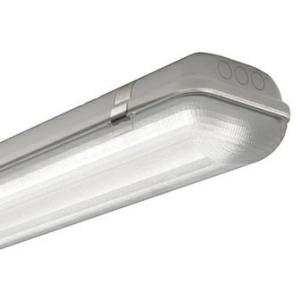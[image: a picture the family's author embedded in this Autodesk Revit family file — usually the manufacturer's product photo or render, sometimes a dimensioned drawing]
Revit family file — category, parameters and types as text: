
# Revit family: 3f_filippi_-_3f_linda_3f_filippi_-_58600_-_3f_linda_led_2x24w_ep_l1270
name_source: partatom
category: Lighting Fixtures
units: mm (PartAtom-declared; Revit-internal decimal feet)

## family parameters
Cut with Voids When Loaded = No
Host = Face
Light Source = No
Part Type = Normal
Room Calculation Point = No
Round Connector Dimension = Use Diameter
Shared = No

## types (1)
- 3F Filippi - 3F Linda (1 x LED, 7911 lm, 55.5 W, 4000 K)
    Apparent Load = 56 VA
    Approval mark = ENEC
    CIE Flux Codes = 46 76 93 97 100
    Color Rendering = 80
    Color Temperature = 4000 K
    Control Gear = Electronic ballast
    Default Elevation = 1800 mm
    Description = ILLUMINOTECHNICAL
Luminous efficiency 100% (DLOR 97%, ULOR 3%).
Initial luminous flux of the luminaire 7911 lm.
Emergency luminaire luminous flux BLF 7.1%.
Controlled symmetric distribution.
Installation Interdistance Transv.D = 1.52 x hu - Long.D = 1.17 x hu.
Tabular UGR (CIE 117 - 4H-8H; S=0.25H; 70/50/20): RUG 24.4 - 23.5.
Beam angle: 94° - 78°.
Luminous efficacy 143 lm/W.
Lifetime (L93/B10): 30000 h. (tq+25°C)
Lifetime (L90/B10): 50000 h. (tq+25°C)
Lifetime (L85/B10): 80000 h. (tq+25°C)
Lifetime (L80/B10): 100000 h. (tq+25°C)
Sudden decreased luminous flux after 50000 hours: 0% (C0).
Photobiological safety in compliance with IEC/TR 62778: RG0 risk exempt, (IEC 62471).
In compliance with IEC/EN 62722-2-1 - IEC/EN 62717 standards.

SOURCE
2 linear LED modules 24W/840.
Energy efficiency class (UE 2019/2020 - UE 2019/2015): D.
CIE 13.3 Colour rendering index: CRI >80 (R9 <50%).
IES TM-30 Fidelity Index: Rf = 84 Rg = 95.
CCT nominal colour temperature 4000 K.
Colour initial tolerance (MacAdam): SDCM 3.

MECHANICAL
Self-extinguishing V2 polycarbonate housing, injection moulded, RAL 7035 grey.
Ecologic anti-aging injected sealing gasket.
Diffuser in self-extinguishing V2 polycarbonate, photo-engraved interior, UV stabilised, injection moulded with smooth outer surface, tamper-proof opening.
Gear-holder reflector in hot-dip galvanised steel, painted with white polyester base.
Snug fit safety snap-lock clips for diffuser mounting in stainless steel, screwdriver opening.
Fixing brackets in stainless steel.
Possibility for technicians to access the interior of the luminaire.
Luminaire with limited surface temperature. - D - (EN 60598-2-24)
Dimensions: 1270x160 mm, height 100 mm. Weight 3.294 kg.
IP66 protection degree.
Mechanical strength to impacts IK10 (20 joule).
Glow-wire test resistance 850°C.

ELECTRICAL
Halogen Free electronic wiring 230V-50/60Hz, power factor 0.90, THD <25%, constant output current, SELV, class I, 1 driver.
Power of the luminaire 55.5 W.
CE - IEC 60598-1 - EN 60598-1.
EP maintained emergency wiring on board, 1h duration, 24h recharge; compliant with EN 60598-2-22, excluding high risk areas.
SAFE FLICKER: PstLM=<1 and SVM=<0.4 (IEC TR 61547-1 and IEC TR 63158), to ensure a more comfortable and safe light.
Ambient temperature from +5°C to +25°C.
Temperature class T6 max 85°C.
Relative humidity UR: <85%.

INSTALLATION
Ceiling / Suspended / Wall.
All accessories dedicated to this product are available on the Catalog and on our website www.3F-Filippi.com.

APPLICATIONS
Suitable product for food production plants (HACCP), IFS (Food Version 6), BRC (GSFS Food Version 7).
Dry, dusty indoor environments, subject to occasional water splashes.
Virtually shatterproof polycarbonate compatibly with the fumes / atmospheres that compromise the elasticity of plastic materials.
Not suitable for installation on surfaces subject to important vibrations, exposed to weather conditions, on ropes or poles.
Suitable for illumination of public car parks and parking grounds referred to DIN 67528:2018-04.

WARNING
Fixture not suitable for cold stores with an ambient temperature <5°C and/or relative humidity >85%.
Luminaire designed for disposal/recycling at end-of-life.
Replaceable (LED only) light source by a professional. Replaceable control gear by a professional.
    Height = 100 mm  [stored 0.328084 ft]
    Lamp = 1 x LED
    Lamp Light Flux = 7911 lm
    Lamp Power = 55.5 W
    Lamp count = 1
    Length = 1270 mm
    Lifetime = 50000 h
    Luminous efficacy = 143 lm/W
    Manufacturer = 3F Filippi
    ModVariant = No
    Model = 3F Filippi - 58600 - 3F Linda LED 2x24W EP L1270
    Mounting Place = Ceiling
    Mounting Type = Pendant
    Number of Poles = 1
    OnlyDefault = Yes
    Power Factor = 1
    Product Name = 3F Filippi - 3F Linda
    Product group = pendant luminaire
    ProductGroupID = 9
    Protection Class = Protection class I
    Protection Degree = IP 66
    RLX_Detail_Level = 1
    RLX_Emergency_Light_Flux = 0 lm
    RLX_Emergency_Type = 0
    RLX_Emergency_Type_DB = No
    RlxData = <blob elided: 71621 chars, md5=804b8fbe>
    Socket = socket
    Standby Power = 0 W
    System Light Flux = 7911 lm
    System Power = 56 W
    Type Comments = Product without accessories
    Type Image = 3ffilippi_3f_linda_led_2x.jpg
    URL = http://relux.com
    VarID = ---
    Voltage = 0 V
    Weight = 0.00 kg
    Width = 160 mm

note: [stored X ft] marks values corroborated as IEEE doubles in the binary element streams (Revit-internal decimal feet)

## geometry (parser evidence)
native form markers: Blend x4, Sweep x8
no freeform markers — native parametric forms only
